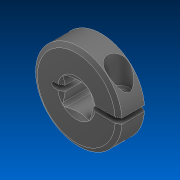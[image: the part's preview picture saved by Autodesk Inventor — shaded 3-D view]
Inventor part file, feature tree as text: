
AUTODESK INVENTOR PART (.ipt)
format: ipt  version: 2022.2 (Build 262287000, 287)  size: 176,640 bytes
history: native  units: in
note: dims shown in document units (in); Inventor stores cm internally (conversion verified against a paired STEP export)
features: mirror x1
ambient origin geometry x8: Origin, YZ Plane, XZ Plane, XY Plane, X Axis, Y Axis, Z Axis, Center Point
bodies: Solid1 (feature_tree)
feature tree (1):
  mirror  "Mirror1"
